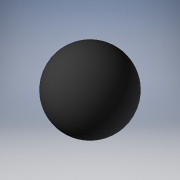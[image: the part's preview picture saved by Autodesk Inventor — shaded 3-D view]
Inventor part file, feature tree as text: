
AUTODESK INVENTOR PART (.ipt)
format: ipt  version: 2019 (Build 230136000, 136)  size: 139,776 bytes
history: native  units: mm
features: other x7, revolve x1, sketch x1
ambient origin geometry x8: Origin, YZ Plane, XZ Plane, XY Plane, X Axis, Y Axis, Z Axis, Center Point
bodies: Solid1 (feature_tree)
feature tree (9):
  revolve  "Revolution1"  [1 undecoded]
  other  "dgbb_ball_XY"
  other  "dgbb_ball_YZ"
  other  "dgbb_ball_ZX"
  other  "dgbb_ball_X"
  other  "dgbb_ball_Y"
  other  "dgbb_ball_Z"
  other  "dgbb_ball_Center"
  sketch  "Sketch_1"  dims[d0=360.0deg]
note: 1 required parameter value undecoded (feature->parameter linkage not recoverable at this tier; creation-order binding heuristic only, values carry confidence <= 0.55)
